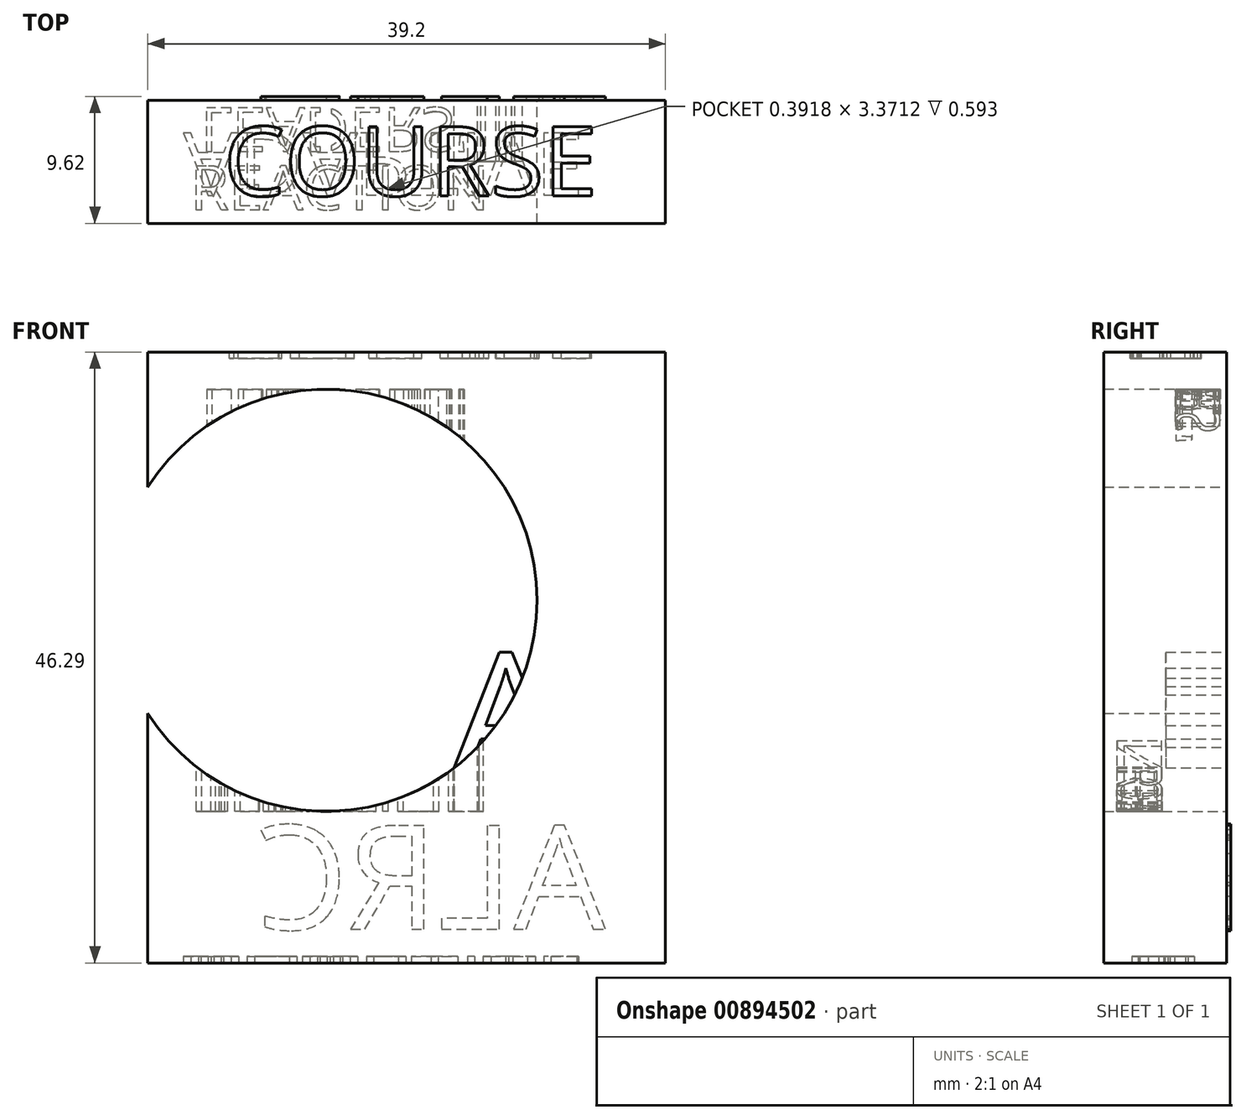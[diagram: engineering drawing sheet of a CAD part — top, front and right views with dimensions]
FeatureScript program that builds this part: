
annotation { "Feature Type Name" : "Feature", "Feature Type Description" : "" }
export const myFeature = defineFeature(function(context is Context, id is Id, definition is map)
    precondition{}
    {
        {
            var Q0;
            Q0=qCreatedBy(makeId("Front.planeOp"),FACE);
            var sketch = newSketch(context, id + "F0", { "sketchPlane" : qUnion([Q0])});
            skLineSegment(sketch, "E0.bottom", {"start": v(-25.45, -31.3) * mm, "end": v(13.75, -31.3) * mm});
            skLineSegment(sketch, "E0.top", {"start": v(-25.45, 15) * mm, "end": v(13.75, 15) * mm});
            skLineSegment(sketch, "E0.left", {"start": v(-25.45, -31.3) * mm, "end": v(-25.45, 15) * mm});
            skLineSegment(sketch, "E0.right", {"start": v(13.75, -31.3) * mm, "end": v(13.75, 15) * mm});
            skSolve(sketch);
        }
        {
            var Q0;
            Q0 = qSketchRegion(id + "F0", true);
            extrude(context, id + "F1", {"entities" : qUnion([Q0]), "depth" : 9.3 * mm, "offsetDistance" : 25.4 * mm});
        }
        {
            var Q0;
            Q0=qCreatedBy(makeId("Front.planeOp"),FACE);
            var sketch = newSketch(context, id + "F2", { "sketchPlane" : qUnion([Q0])});
            skCircle(sketch, "E1", {"center": v(-11.95, -3.8) * mm, "radius": 16 * mm});
            skSolve(sketch);
        }
        {
            var Q0;
            Q0 = qSketchRegion(id + "F2", true);
            extrude(context, id + "F3", {"entities" : qUnion([Q0]), "operationType" : NewBodyOperationType.REMOVE, "depth" : 23.5 * mm, "offsetDistance" : 25.4 * mm});
        }
        {
            var Q0;
            Q0=makeQuery(id+"F1.opExtrude","CAP_FACE",FACE,{"disambiguationData":[OSD([sQuery(id+"F0.wireOp",EDGE,"E0.bottom"),sQuery(id+"F0.wireOp",EDGE,"E0.top"),sQuery(id+"F0.wireOp",EDGE,"E0.left"),sQuery(id+"F0.wireOp",EDGE,"E0.right")])],"isStart":true});
            var sketch = newSketch(context, id + "F4", { "sketchPlane" : qUnion([Q0])});
            skText(sketch, "E2", { "text": "ALRC", "fontName": "OpenSans-Regular.ttf"});
            const initialGuessF4  = {"E2": [-0.00922, -0.02874, 1, 0, 0.00793]};
            skSetInitialGuess(sketch, initialGuessF4);
            skSolve(sketch);
        }
        {
            var Q0;
            Q0 = qSketchRegion(id + "F4", true);
            extrude(context, id + "F5", {"entities" : qUnion([Q0]), "operationType" : NewBodyOperationType.ADD, "depth" : 0.31 * mm, "offsetDistance" : 25.4 * mm});
        }
        {
            var Q0;
            {var subQ0=sQuery(id+"F0.wireOp",EDGE,"E0.right");var subQ1=sQuery(id+"F0.wireOp",EDGE,"E0.left");var subQ2=sQuery(id+"F0.wireOp",EDGE,"E0.top");var subQ3=sQuery(id+"F0.wireOp",EDGE,"E0.bottom");Q0=makeQuery(id+"F5.boolean.opBoolean","SPLIT",FACE,{"disambiguationData":[TD([makeQuery(id+"F1.opExtrude","SWEPT_FACE",FACE,{"disambiguationData":[OSD([subQ3])]})])],"derivedFrom":makeQuery(id+"F1.opExtrude","CAP_FACE",FACE,{"disambiguationData":[OSD([subQ3,subQ2,subQ1,subQ0])],"isStart":true})});}
            var sketch = newSketch(context, id + "F6", { "sketchPlane" : qUnion([Q0])});
            skText(sketch, "E3", { "text": "A", "fontName": "OpenSans-Regular.ttf"});
            const initialGuessF6  = {"E3": [-0.00591, -0.01734, 1, 0, 0.00964]};
            skSetInitialGuess(sketch, initialGuessF6);
            skSolve(sketch);
        }
        {
            var Q0;
            Q0 = qSketchRegion(id + "F6", true);
            extrude(context, id + "F7", {"entities" : qUnion([Q0]), "operationType" : NewBodyOperationType.ADD, "oppositeDirection" : true, "depth" : 4.62 * mm, "offsetDistance" : 25.4 * mm});
        }
        {
            var Q0;
            Q0=makeQuery(id+"F1.opExtrude","CAP_FACE",FACE,{"disambiguationData":[OSD([sQuery(id+"F0.wireOp",EDGE,"E0.bottom"),sQuery(id+"F0.wireOp",EDGE,"E0.top"),sQuery(id+"F0.wireOp",EDGE,"E0.left"),sQuery(id+"F0.wireOp",EDGE,"E0.right")])],"isStart":false});
            var sketch = newSketch(context, id + "F8", { "sketchPlane" : qUnion([Q0])});
            skLineSegment(sketch, "E4", {"start": v(8.55, 9.37) * mm, "end": v(8.55, -25.94) * mm});
            skLineSegment(sketch, "E5", {"start": v(8.55, -25.94) * mm, "end": v(-8.36, -25.94) * mm});
            skSolve(sketch);
        }
        {
            var Q0;
            {var subQ4=sQuery(id+"F0.wireOp",EDGE,"E0.bottom");Q0=makeQuery(id+"F8.imprint","IMPRINT",FACE,{"disambiguationData":[TD([[makeQuery(id+"F8.imprint","IMPRINT",EDGE,{"derivedFrom":makeQuery(id+"F1.opExtrude","CAP_EDGE",EDGE,{"disambiguationData":[OSD([subQ4])],"isStart":false})}),1.0]])]});}
            var sketch = newSketch(context, id + "F9", { "sketchPlane" : qUnion([Q0])});
            skLineSegment(sketch, "E6", {"start": v(-8.32, -25.96) * mm, "end": v(-8.32, -28.4) * mm});
            skSolve(sketch);
        }
        {
            var Q0;
            Q0=makeQuery(id+"F1.opExtrude","SWEPT_FACE",FACE,{"disambiguationData":[OSD([sQuery(id+"F0.wireOp",EDGE,"E0.bottom")])]});
            var sketch = newSketch(context, id + "F10", { "sketchPlane" : qUnion([Q0])});
            skText(sketch, "E7", { "text": "ADAPTIVE", "fontName": "OpenSans-Regular.ttf"});
            const initialGuessF10  = {"E7": [-0.02276, 0.00245, 1, 0, 0.00477]};
            skSetInitialGuess(sketch, initialGuessF10);
            skSolve(sketch);
        }
        {
            var Q0;
            Q0 = qSketchRegion(id + "F10", true);
            extrude(context, id + "F11", {"entities" : qUnion([Q0]), "operationType" : NewBodyOperationType.REMOVE, "oppositeDirection" : true, "depth" : 0.5 * mm, "offsetDistance" : 25.4 * mm});
        }
        {
            var Q0;
            Q0=makeQuery(id+"F1.opExtrude","SWEPT_FACE",FACE,{"disambiguationData":[OSD([sQuery(id+"F0.wireOp",EDGE,"E0.top")])]});
            var sketch = newSketch(context, id + "F12", { "sketchPlane" : qUnion([Q0])});
            skText(sketch, "E8", { "text": "COURSE", "fontName": "OpenSans-Regular.ttf"});
            const initialGuessF12  = {"E8": [-0.0197, -0.00723, 1, 0, 0.00528]};
            skSetInitialGuess(sketch, initialGuessF12);
            skSolve(sketch);
        }
        {
            var Q0;
            Q0 = qSketchRegion(id + "F12", true);
            extrude(context, id + "F13", {"entities" : qUnion([Q0]), "operationType" : NewBodyOperationType.REMOVE, "oppositeDirection" : true, "depth" : 0.5 * mm, "offsetDistance" : 25.4 * mm});
        }
        {
            var Q0;
            Q0=qCreatedBy(makeId("Top.planeOp"),FACE);
            var sketch = newSketch(context, id + "F14", { "sketchPlane" : qUnion([Q0])});
            skText(sketch, "E9", { "text": "REACTION", "fontName": "OpenSans-Regular.ttf"});
            const initialGuessF14  = {"E9": [-0.02223, -0.0083, 1, 0, 0.0034]};
            skSetInitialGuess(sketch, initialGuessF14);
            skSolve(sketch);
        }
        {
            var Q0;
            Q0 = qSketchRegion(id + "F14", true);
            extrude(context, id + "F15", {"entities" : qUnion([Q0]), "operationType" : NewBodyOperationType.REMOVE, "oppositeDirection" : true, "depth" : 19.8 * mm, "offsetDistance" : 25.4 * mm});
        }
        {
            var Q0;
            {var subQ1=sQuery(id+"F0.wireOp",EDGE,"E0.left");var subQ2=sQuery(id+"F0.wireOp",EDGE,"E0.top");Q0=makeQuery(id+"F3.boolean.opBoolean","SPLIT",FACE,{"disambiguationData":[TD([makeQuery(id+"F1.opExtrude","SWEPT_FACE",FACE,{"disambiguationData":[OSD([subQ2])]})])],"derivedFrom":makeQuery(id+"F1.opExtrude","SWEPT_FACE",FACE,{"disambiguationData":[OSD([subQ1])]})});}
            var sketch = newSketch(context, id + "F16", { "sketchPlane" : qUnion([Q0])});
            skLineSegment(sketch, "E10.bottom", {"start": v(0.05, 2.3) * mm, "end": v(4.33, 2.3) * mm});
            skLineSegment(sketch, "E10.top", {"start": v(0.05, -2) * mm, "end": v(4.33, -2) * mm});
            skLineSegment(sketch, "E10.left", {"start": v(0.05, 2.3) * mm, "end": v(0.05, -2) * mm});
            skLineSegment(sketch, "E10.right", {"start": v(4.33, 2.3) * mm, "end": v(4.33, -2) * mm});
            skSolve(sketch);
        }
        {
            var Q0;
            Q0=sQuery(id+"F16.wireOp",EDGE,"E10.right");
            var Q1;
            Q1=sQuery(id+"F16.wireOp",EDGE,"E10.bottom");
            var Q2;
            Q2=sQuery(id+"F16.wireOp",EDGE,"E10.left");
            var Q3;
            Q3=sQuery(id+"F16.wireOp",EDGE,"E10.top");
            extrude(context, id + "F17", {"bodyType" : ToolBodyType.SURFACE, "surfaceEntities" : qUnion([Q0, Q1, Q2, Q3]), "oppositeDirection" : true, "depth" : 0 * mm, "offsetDistance" : 25.4 * mm});
        }
        {
            var Q0;
            Q0=makeQuery(id+"F17.opExtrude","SWEPT_FACE",FACE,{"disambiguationData":[OSD([sQuery(id+"F16.wireOp",EDGE,"E10.top")])]});
            var sketch = newSketch(context, id + "F18", { "sketchPlane" : qUnion([Q0])});
            skText(sketch, "E11", { "text": "LEADERS\'", "fontName": "OpenSans-Regular.ttf"});
            const initialGuessF18  = {"E11": [-0.02145, 0.00055, 1, 0, 0.00333]};
            skSetInitialGuess(sketch, initialGuessF18);
            skSolve(sketch);
        }
        {
            var Q0;
            Q0 = qSketchRegion(id + "F18", true);
            extrude(context, id + "F19", {"entities" : qUnion([Q0]), "operationType" : NewBodyOperationType.REMOVE, "oppositeDirection" : true, "depth" : 14.18 * mm, "offsetDistance" : 25.4 * mm});
        }
    });
